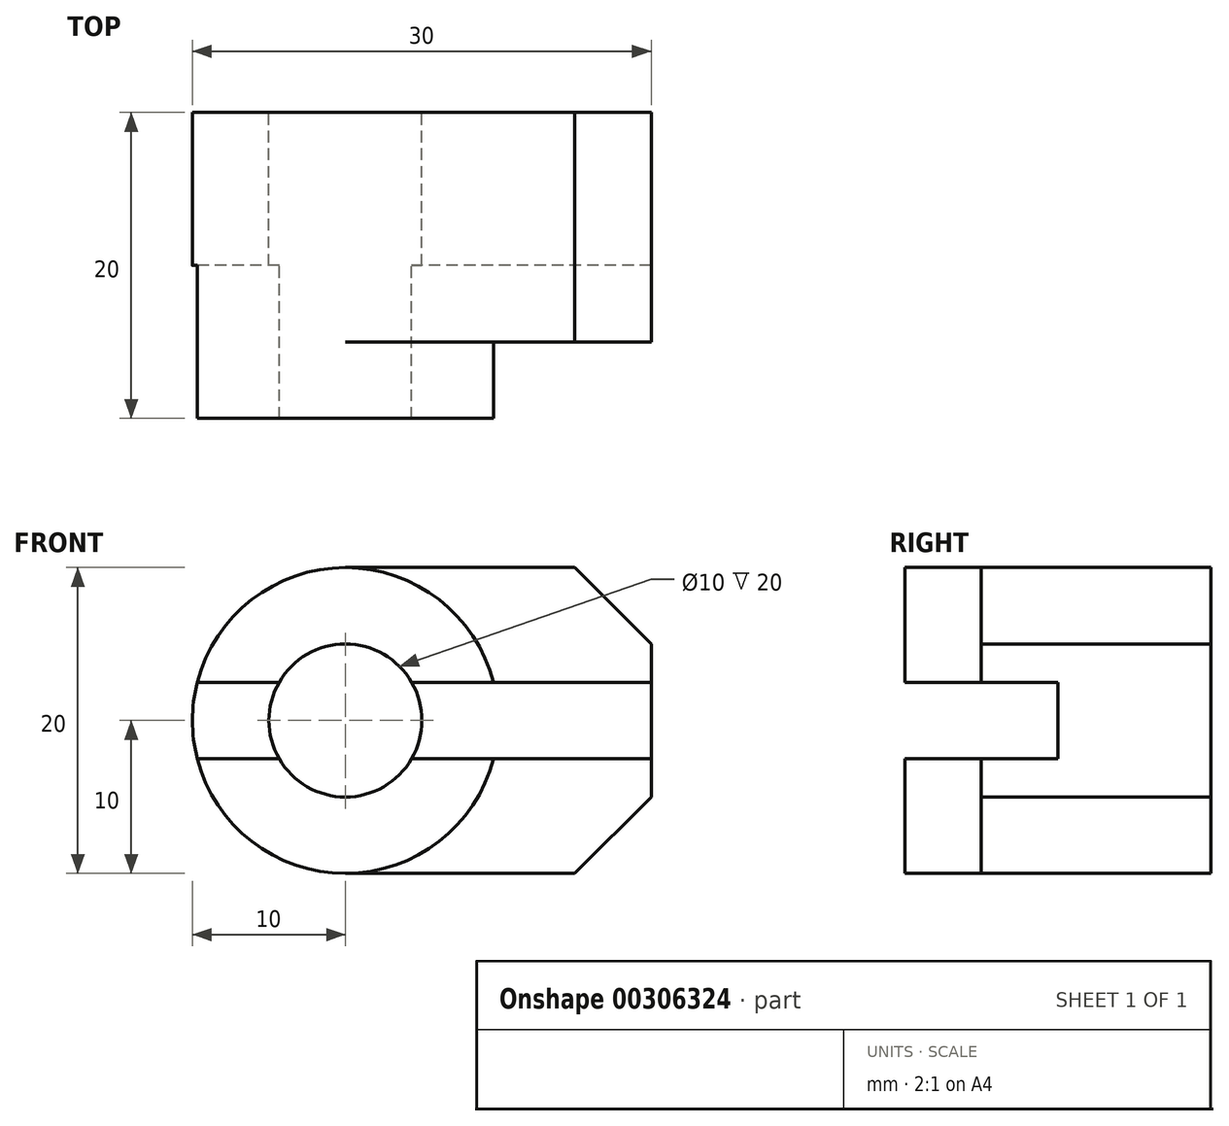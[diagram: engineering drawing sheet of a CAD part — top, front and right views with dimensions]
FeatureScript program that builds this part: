
annotation { "Feature Type Name" : "Feature", "Feature Type Description" : "" }
export const myFeature = defineFeature(function(context is Context, id is Id, definition is map)
    precondition{}
    {
        {
            var Q0;
            Q0=qCreatedBy(makeId("Front.planeOp"),FACE);
            var sketch = newSketch(context, id + "F0", { "sketchPlane" : qUnion([Q0])});
            skCircle(sketch, "E0", {"center": v(0, 0) * mm, "radius": 5 * mm});
            skCircle(sketch, "E1", {"center": v(0, 0) * mm, "radius": 10 * mm});
            skLineSegment(sketch, "E2", {"start": v(0, 10) * mm, "end": v(15, 10) * mm});
            skLineSegment(sketch, "E3", {"start": v(15, 10) * mm, "end": v(20, 5) * mm});
            skLineSegment(sketch, "E4", {"start": v(20, 5) * mm, "end": v(20, -5) * mm});
            skLineSegment(sketch, "E5", {"start": v(0, -10) * mm, "end": v(15, -10) * mm});
            skLineSegment(sketch, "E6", {"start": v(15, -10) * mm, "end": v(20, -5) * mm});
            skSolve(sketch);
        }
        {
            var Q0;
            Q0 = qSketchRegion(id + "F0", true);
            extrude(context, id + "F1", {"entities" : qUnion([Q0]), "depth" : 20 * mm});
        }
        {
            var Q0;
            Q0=makeQuery(id+"F1.opExtrude","CAP_FACE",FACE,{"disambiguationData":[OSD([sQuery(id+"F0.wireOp",EDGE,"E0"),sQuery(id+"F0.wireOp",EDGE,"E1"),sQuery(id+"F0.wireOp",EDGE,"E2"),sQuery(id+"F0.wireOp",EDGE,"E3"),sQuery(id+"F0.wireOp",EDGE,"E4"),sQuery(id+"F0.wireOp",EDGE,"E5"),sQuery(id+"F0.wireOp",EDGE,"E6")])],"isStart":false});
            var sketch = newSketch(context, id + "F2", { "sketchPlane" : qUnion([Q0])});
            skLineSegment(sketch, "E7", {"start": v(20, 2.5) * mm, "end": v(20, -2.5) * mm});
            skLineSegment(sketch, "E8", {"start": v(20, -2.5) * mm, "end": v(-10, -2.5) * mm});
            skLineSegment(sketch, "E9", {"start": v(-10, -2.5) * mm, "end": v(-10, 2.5) * mm});
            skLineSegment(sketch, "E10", {"start": v(-10, 2.5) * mm, "end": v(20, 2.5) * mm});
            skSolve(sketch);
        }
        {
            var Q0;
            Q0 = qSketchRegion(id + "F2", true);
            extrude(context, id + "F3", {"entities" : qUnion([Q0]), "operationType" : NewBodyOperationType.REMOVE, "oppositeDirection" : true, "depth" : 10 * mm});
        }
        {
            var Q0;
            {var subQ0=sQuery(id+"F0.wireOp",EDGE,"E2");var subQ1=sQuery(id+"F0.wireOp",EDGE,"E1");var subQ2=sQuery(id+"F0.wireOp",EDGE,"E3");var subQ3=sQuery(id+"F0.wireOp",EDGE,"E0");var subQ4=sQuery(id+"F0.wireOp",EDGE,"E4");Q0=makeQuery(id+"F3.boolean.opBoolean","SPLIT",FACE,{"disambiguationData":[TD([makeQuery(id+"F1.opExtrude","SWEPT_FACE",FACE,{"disambiguationData":[OSD([subQ0])]})])],"derivedFrom":makeQuery(id+"F1.opExtrude","CAP_FACE",FACE,{"disambiguationData":[OSD([subQ3,subQ1,subQ0,subQ2,subQ4,sQuery(id+"F0.wireOp",EDGE,"E5"),sQuery(id+"F0.wireOp",EDGE,"E6")])],"isStart":false})});}
            var sketch = newSketch(context, id + "F4", { "sketchPlane" : qUnion([Q0])});
            skArc(sketch, "E11", {"start": v(0, -10) * mm, "mid": v(10, 0) * mm, "end": v(0, 10) * mm});
            skLineSegment(sketch, "E12", {"start": v(0, 10) * mm, "end": v(15, 10) * mm});
            skLineSegment(sketch, "E13", {"start": v(15, 10) * mm, "end": v(20, 5) * mm});
            skLineSegment(sketch, "E14", {"start": v(20, 5) * mm, "end": v(20, -5) * mm});
            skLineSegment(sketch, "E15", {"start": v(0, -10) * mm, "end": v(15, -10) * mm});
            skLineSegment(sketch, "E16", {"start": v(15, -10) * mm, "end": v(20, -5) * mm});
            skSolve(sketch);
        }
        {
            var Q0;
            Q0 = qSketchRegion(id + "F4", true);
            extrude(context, id + "F5", {"entities" : qUnion([Q0]), "operationType" : NewBodyOperationType.REMOVE, "oppositeDirection" : true, "depth" : 5 * mm});
        }
    });
